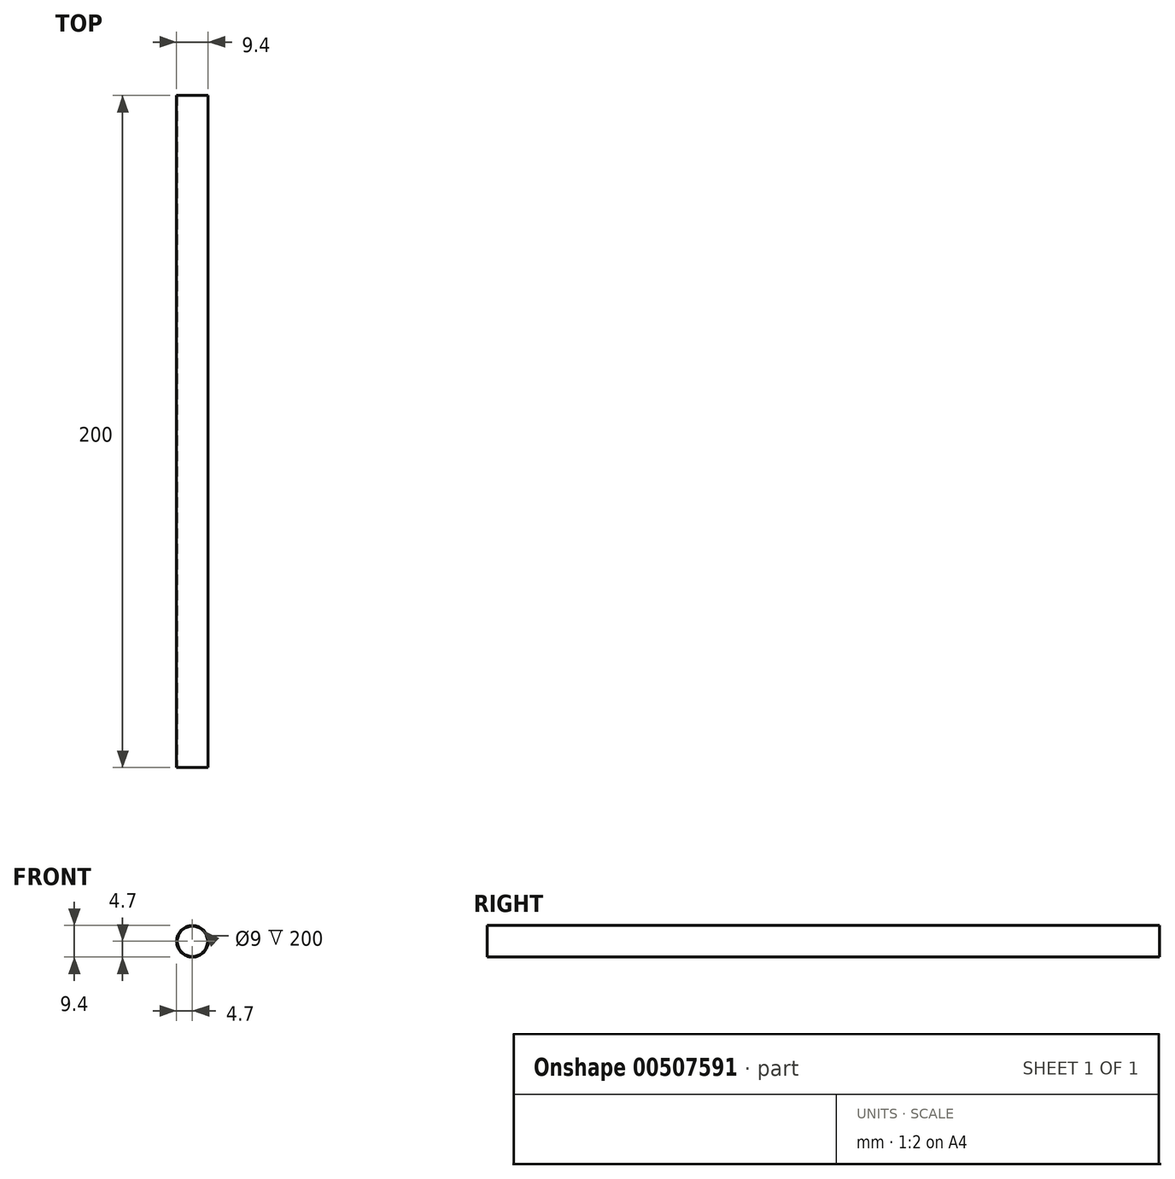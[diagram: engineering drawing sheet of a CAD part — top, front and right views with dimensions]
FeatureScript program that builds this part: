
annotation { "Feature Type Name" : "Feature", "Feature Type Description" : "" }
export const myFeature = defineFeature(function(context is Context, id is Id, definition is map)
    precondition{}
    {
        {
            var Q0;
            Q0=qCreatedBy(makeId("Front.planeOp"),FACE);
            var sketch = newSketch(context, id + "F0", { "sketchPlane" : qUnion([Q0])});
            skCircle(sketch, "E0", {"center": v(0, 0) * mm, "radius": 4.7 * mm});
            skCircle(sketch, "E1", {"center": v(0, 0) * mm, "radius": 4.5 * mm});
            skLineSegment(sketch, "E2", {"start": v(0, 4.7) * mm, "end": v(0, -4.7) * mm, "construction": true});
            skLineSegment(sketch, "E3", {"start": v(-4.7, 0) * mm, "end": v(4.7, 0) * mm, "construction": true});
            skSolve(sketch);
        }
        {
            var Q0;
            Q0=makeQuery(id+"F0.imprint","IMPRINT",FACE,{"disambiguationData":[TD([[makeQuery(id+"F0.imprint","IMPRINT",EDGE,{"derivedFrom":sQuery(id+"F0.wireOp",EDGE,"E0")}),1.0]])]});
            extrude(context, id + "F1", {"entities" : qUnion([Q0]), "oppositeDirection" : true, "depth" : 200 * mm});
        }
        {
            var Q0;
            Q0=qCreatedBy(makeId("Right.planeOp"),FACE);
            cPlane(context, id + "F2", {"entities" : qUnion([Q0]), "cplaneType" : CPlaneType.OFFSET, "offset" : 15 * mm, "oppositeDirection" : true, "width" : 150 * mm, "height" : 150 * mm});
        }
        {
            var Q0;
            Q0=makeQuery(id+"F1.opExtrude","SWEPT_BODY",BODY,{"disambiguationData":[OSD([sQuery(id+"F0.wireOp",EDGE,"E0"),sQuery(id+"F0.wireOp",EDGE,"E1")])]});
            var Q1;
            Q1=qCreatedBy(id+"F2.planeOp",FACE);
            mirror(context, id + "F3", {"entities" : qUnion([Q0]), "mirrorPlane" : qUnion([Q1])});
        }
        {
            var Q0;
            Q0=makeQuery(id+"F3.opPattern","COPY",BODY,{"derivedFrom":makeQuery(id+"F1.opExtrude","SWEPT_BODY",BODY,{"disambiguationData":[OSD([sQuery(id+"F0.wireOp",EDGE,"E0"),sQuery(id+"F0.wireOp",EDGE,"E1")])]}),"instanceName":"1"});
            deleteBodies(context, id + "F4", {"entities" : qUnion([Q0])});
        }
    });
